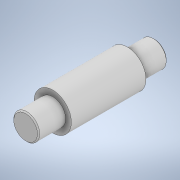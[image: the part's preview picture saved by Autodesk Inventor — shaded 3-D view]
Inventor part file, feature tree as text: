
AUTODESK INVENTOR PART (.ipt)
format: ipt  version: 2021 (Build 250183000, 183)  size: 122,368 bytes
history: native  units: mm
features: revolve x1, sketch x1
ambient origin geometry x8: Origin, YZ Plane, XZ Plane, XY Plane, X Axis, Y Axis, Z Axis, Center Point
bodies: Solid1 (feature_tree)
feature tree (2):
  revolve  "Revolution1"  [1 undecoded]
  sketch  "Sketch1"  dims[d0=23.0mm d1=16.0mm d2=3.5mm d3=23.0mm d4=16.0mm d5=1.0mm d6=1.0mm d7=11.5mm d8=90.0deg]
note: 1 required parameter value undecoded (feature->parameter linkage not recoverable at this tier; creation-order binding heuristic only, values carry confidence <= 0.55)
